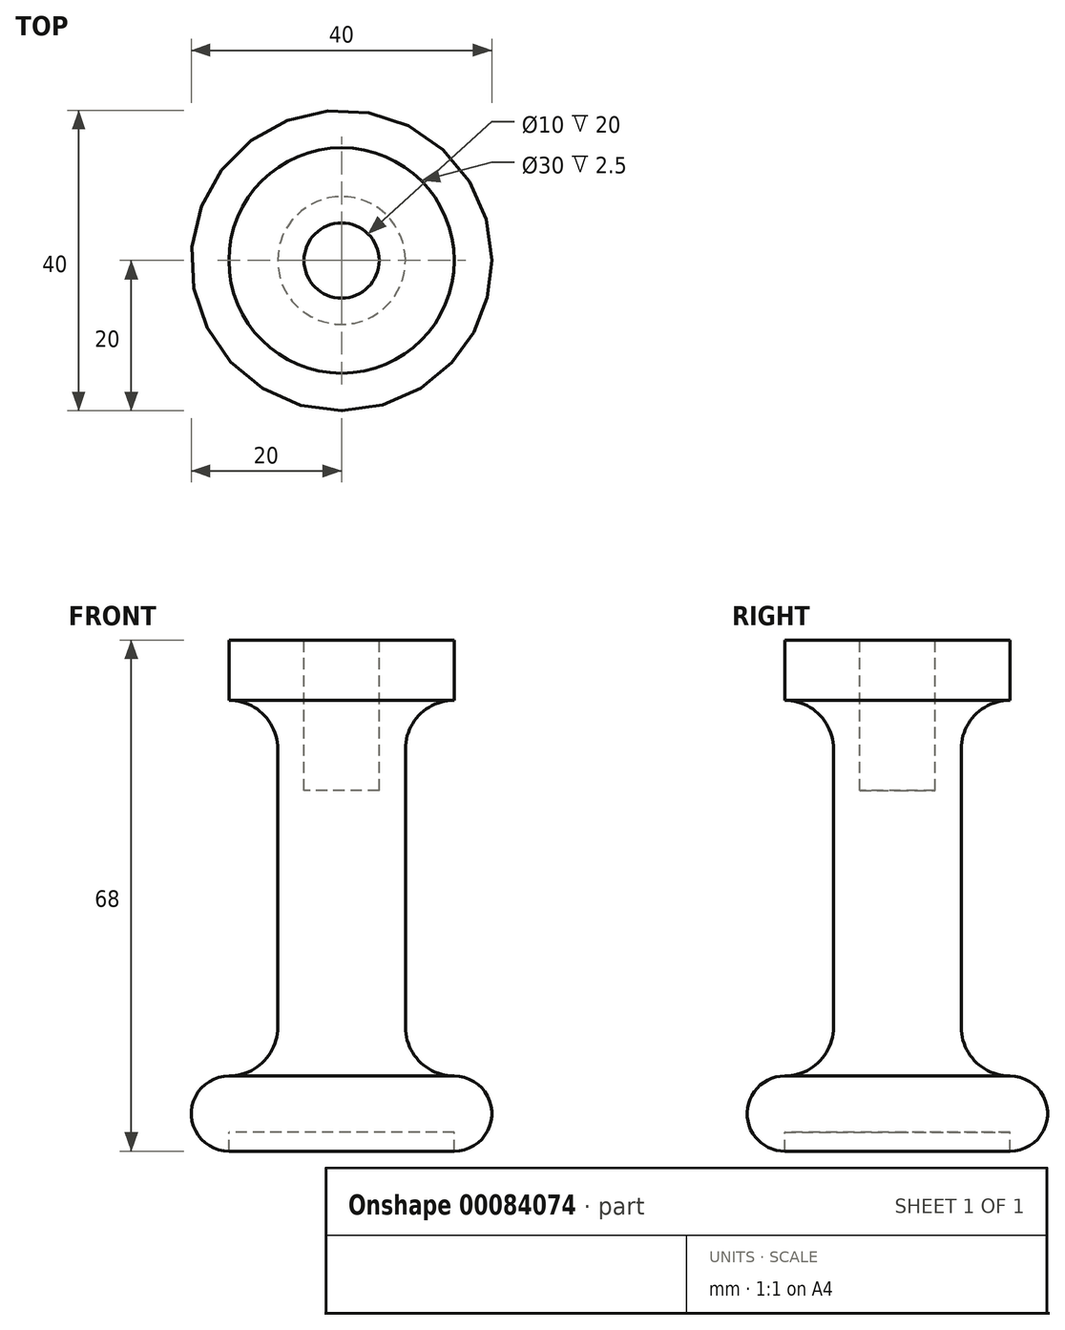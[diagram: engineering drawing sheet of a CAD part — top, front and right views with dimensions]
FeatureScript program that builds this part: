
annotation { "Feature Type Name" : "Feature", "Feature Type Description" : "" }
export const myFeature = defineFeature(function(context is Context, id is Id, definition is map)
    precondition{}
    {
        {
            var Q0;
            Q0=qCreatedBy(makeId("Front.planeOp"),FACE);
            var sketch = newSketch(context, id + "F0", { "sketchPlane" : qUnion([Q0])});
            skLineSegment(sketch, "E0", {"start": v(5, 48) * mm, "end": v(0, 48) * mm});
            skLineSegment(sketch, "E1", {"start": v(0, 48) * mm, "end": v(0, 2.5) * mm});
            skLineSegment(sketch, "E2", {"start": v(0, 2.5) * mm, "end": v(15, 2.5) * mm});
            skLineSegment(sketch, "E3", {"start": v(15, 2.5) * mm, "end": v(15, 0) * mm});
            skArc(sketch, "E4", {"start": v(15, 0) * mm, "mid": v(20, 5) * mm, "end": v(15, 10) * mm});
            skPoint(sketch, "E4.endSnap0", {"position": v(15, 1.25) * mm});
            skArc(sketch, "E5", {"start": v(8.5, 16.5) * mm, "mid": v(10.4, 11.9) * mm, "end": v(15, 10) * mm});
            skLineSegment(sketch, "E6", {"start": v(8.5, 16.5) * mm, "end": v(8.5, 53.5) * mm});
            skArc(sketch, "E7", {"start": v(15, 60) * mm, "mid": v(10.4, 58.1) * mm, "end": v(8.5, 53.5) * mm});
            skLineSegment(sketch, "E8", {"start": v(15, 60) * mm, "end": v(15, 68) * mm});
            skLineSegment(sketch, "E9", {"start": v(15, 68) * mm, "end": v(5, 68) * mm});
            skLineSegment(sketch, "E10", {"start": v(5, 68) * mm, "end": v(5, 48) * mm});
            skSolve(sketch);
        }
        {
            var Q0;
            Q0=makeQuery(id+"F0.imprint","IMPRINT",FACE,{"disambiguationData":[TD([[makeQuery(id+"F0.imprint","IMPRINT",EDGE,{"derivedFrom":sQuery(id+"F0.wireOp",EDGE,"E0")}),1.0]])]});
            var Q1;
            Q1=sQuery(id+"F0.wireOp",EDGE,"E1");
            revolve(context, id + "F1", {"entities" : qUnion([Q0]), "axis" : qUnion([Q1]), "revolveType" : RevolveType.FULL});
        }
    });
